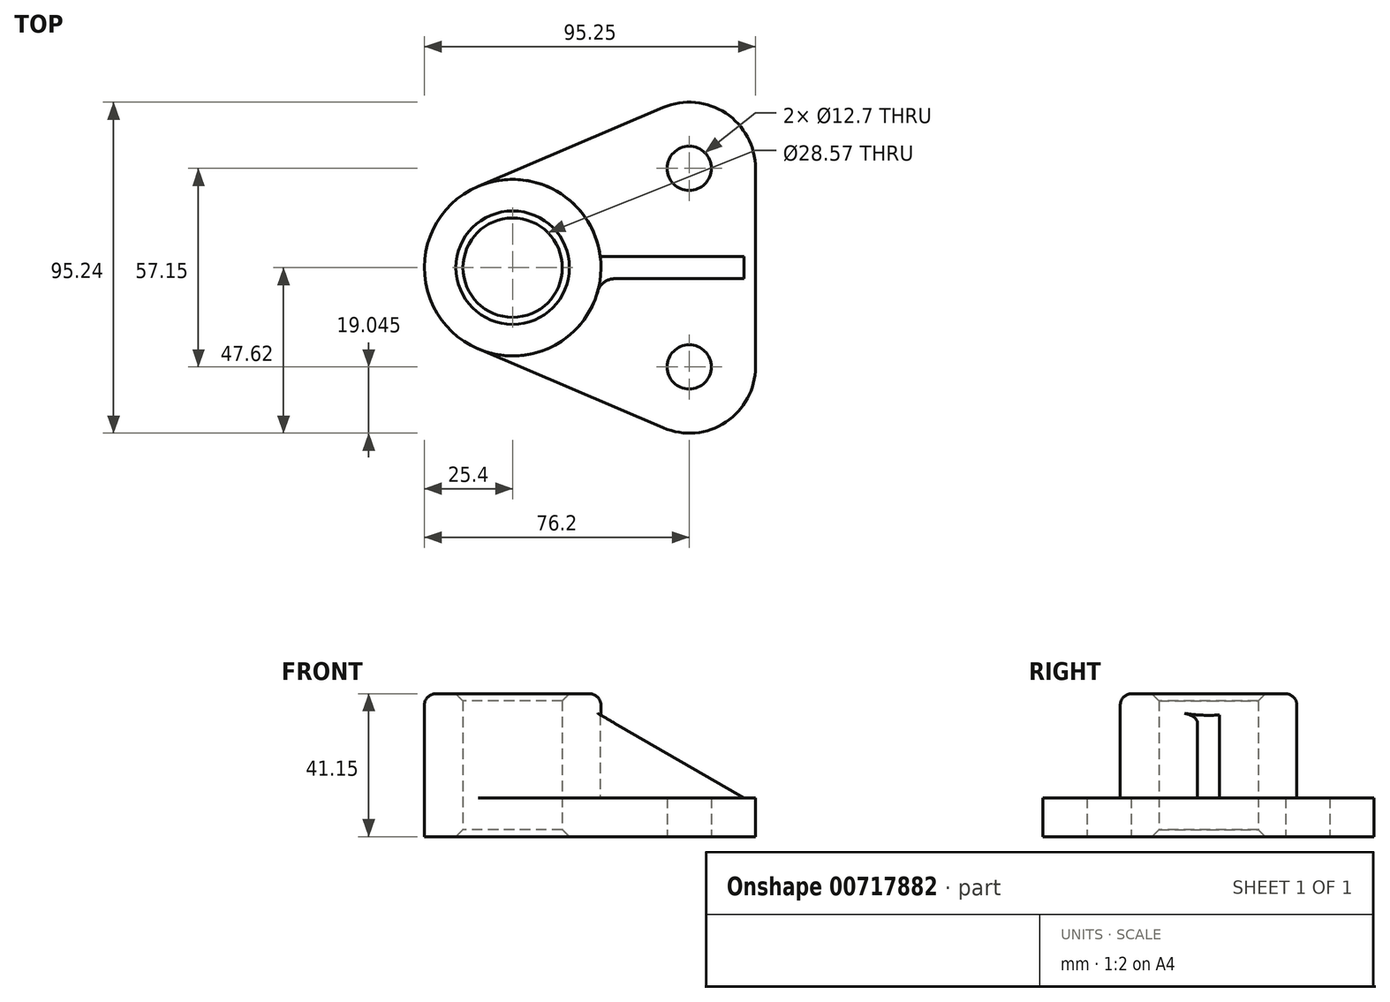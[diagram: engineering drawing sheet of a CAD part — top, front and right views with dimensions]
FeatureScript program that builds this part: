
annotation { "Feature Type Name" : "Feature", "Feature Type Description" : "" }
export const myFeature = defineFeature(function(context is Context, id is Id, definition is map)
    precondition{}
    {
        {
            var Q0;
            Q0=qCreatedBy(makeId("Top.planeOp"),FACE);
            var sketch = newSketch(context, id + "F0", { "sketchPlane" : qUnion([Q0])});
            skCircle(sketch, "E0", {"center": v(0, 0) * mm, "radius": 25.4 * mm});
            skCircle(sketch, "E1", {"center": v(0, 0) * mm, "radius": 14.29 * mm});
            skLineSegment(sketch, "E2", {"start": v(0, 0) * mm, "end": v(75.31, 0) * mm, "construction": true});
            skCircle(sketch, "E3", {"center": v(50.8, -28.58) * mm, "radius": 6.35 * mm});
            skArc(sketch, "E4", {"start": v(43.33, -46.1) * mm, "mid": v(61.3, -44.47) * mm, "end": v(69.85, -28.58) * mm});
            skArc(sketch, "E5.MirrorC", {"start": v(43.33, 46.1) * mm, "mid": v(61.3, 44.47) * mm, "end": v(69.85, 28.58) * mm});
            skCircle(sketch, "E6.MirrorC", {"center": v(50.8, 28.58) * mm, "radius": 6.35 * mm});
            skLineSegment(sketch, "E7", {"start": v(-9.97, 23.36) * mm, "end": v(43.33, 46.1) * mm});
            skLineSegment(sketch, "E8.MirrorCS", {"start": v(-9.97, -23.36) * mm, "end": v(43.33, -46.1) * mm});
            skLineSegment(sketch, "E9", {"start": v(69.85, 28.58) * mm, "end": v(69.85, -28.58) * mm});
            skSolve(sketch);
        }
        {
            var Q0;
            Q0=makeQuery(id+"F0.imprint","IMPRINT",FACE,{"disambiguationData":[TD([[makeQuery(id+"F0.imprint","IMPRINT",EDGE,{"derivedFrom":sQuery(id+"F0.wireOp",EDGE,"E1")}),-1.0]])]});
            extrude(context, id + "F1", {"entities" : qUnion([Q0]), "depth" : 41.15 * mm, "offsetDistance" : 25.4 * mm});
        }
        {
            var Q0;
            Q0=makeQuery(id+"F0.imprint","IMPRINT",FACE,{"disambiguationData":[TD([[makeQuery(id+"F0.imprint","IMPRINT",EDGE,{"derivedFrom":sQuery(id+"F0.wireOp",EDGE,"E3")}),-1.0]])]});
            extrude(context, id + "F2", {"entities" : qUnion([Q0]), "operationType" : NewBodyOperationType.ADD, "depth" : 11.18 * mm, "offsetDistance" : 25.4 * mm});
        }
        {
            var Q0;
            Q0=qCreatedBy(makeId("Front.planeOp"),FACE);
            var sketch = newSketch(context, id + "F3", { "sketchPlane" : qUnion([Q0])});
            skLineSegment(sketch, "E10", {"start": v(66.55, 11.18) * mm, "end": v(69.85, 11.18) * mm});
            skLineSegment(sketch, "E11", {"start": v(66.55, 11.18) * mm, "end": v(24.18, 11.18) * mm});
            skLineSegment(sketch, "E12", {"start": v(66.55, 11.18) * mm, "end": v(24.18, 35.64) * mm});
            skLineSegment(sketch, "E13", {"start": v(24.18, 35.64) * mm, "end": v(24.18, 11.18) * mm});
            skSolve(sketch);
        }
        {
            var Q0;
            Q0=makeQuery(id+"F3.imprint","IMPRINT",FACE,{"disambiguationData":[TD([[makeQuery(id+"F3.imprint","IMPRINT",EDGE,{"derivedFrom":sQuery(id+"F3.wireOp",EDGE,"E11")}),-1.0]])]});
            extrude(context, id + "F4", {"entities" : qUnion([Q0]), "operationType" : NewBodyOperationType.ADD, "depth" : 3.17 * mm, "offsetDistance" : 25.4 * mm});
        }
        {
            var Q0;
            Q0=makeQuery(id+"F1.opExtrude","SWEPT_BODY",BODY,{"disambiguationData":[OSD([sQuery(id+"F0.wireOp",EDGE,"E0"),sQuery(id+"F0.wireOp",EDGE,"E1")])]});
            var Q1;
            Q1=qCreatedBy(makeId("Front.planeOp"),FACE);
            mirror(context, id + "F5", {"operationType" : NewBodyOperationType.ADD, "entities" : qUnion([Q0]), "mirrorPlane" : qUnion([Q1])});
        }
        {
            var Q0;
            {var subQ0=sQuery(id+"F0.wireOp",EDGE,"E0");var subQ1=sQuery(id+"F0.wireOp",EDGE,"E8.MirrorCS");Q0=makeQuery(id+"F4.boolean.opBoolean","SPLIT",EDGE,{"disambiguationData":[TD([makeQuery(id+"F2.opExtrude","SWEPT_FACE",FACE,{"disambiguationData":[OSD([subQ1])]})])],"derivedFrom":makeQuery(id+"F2.opExtrude","CAP_EDGE",EDGE,{"disambiguationData":[OSD([subQ0])],"isStart":false})});}
            var Q1;
            {var subQ0=sQuery(id+"F0.wireOp",EDGE,"E0");var subQ1=sQuery(id+"F0.wireOp",EDGE,"E7");Q1=makeQuery(id+"F4.boolean.opBoolean","SPLIT",EDGE,{"disambiguationData":[TD([makeQuery(id+"F2.opExtrude","SWEPT_FACE",FACE,{"disambiguationData":[OSD([subQ1])]})])],"derivedFrom":makeQuery(id+"F2.opExtrude","CAP_EDGE",EDGE,{"disambiguationData":[OSD([subQ0])],"isStart":false})});}
            var Q2;
            Q2=makeQuery(id+"F4.boolean.opBoolean","INTERSECT",EDGE,{"derivedFrom":[makeQuery(id+"F1.opExtrude","SWEPT_FACE",FACE,{"disambiguationData":[OSD([sQuery(id+"F0.wireOp",EDGE,"E0")])]}),makeQuery(id+"F4.opExtrude","CAP_FACE",FACE,{"disambiguationData":[OSD([sQuery(id+"F3.wireOp",EDGE,"E11"),sQuery(id+"F3.wireOp",EDGE,"E12"),sQuery(id+"F3.wireOp",EDGE,"E13")])],"isStart":false})]});
            var Q3;
            Q3=makeQuery(id+"F4.opExtrude","CAP_EDGE",EDGE,{"disambiguationData":[OSD([sQuery(id+"F3.wireOp",EDGE,"E11")])],"isStart":false});
            var Q4;
            Q4=makeQuery(id+"F5.opPattern","COPY",EDGE,{"derivedFrom":makeQuery(id+"F4.boolean.opBoolean","INTERSECT",EDGE,{"derivedFrom":[makeQuery(id+"F1.opExtrude","SWEPT_FACE",FACE,{"disambiguationData":[OSD([sQuery(id+"F0.wireOp",EDGE,"E0")])]}),makeQuery(id+"F4.opExtrude","CAP_FACE",FACE,{"disambiguationData":[OSD([sQuery(id+"F3.wireOp",EDGE,"E11"),sQuery(id+"F3.wireOp",EDGE,"E12"),sQuery(id+"F3.wireOp",EDGE,"E13")])],"isStart":false})]}),"instanceName":"1"});
            var Q5;
            Q5=makeQuery(id+"F5.opPattern","COPY",EDGE,{"derivedFrom":makeQuery(id+"F4.opExtrude","CAP_EDGE",EDGE,{"disambiguationData":[OSD([sQuery(id+"F3.wireOp",EDGE,"E11")])],"isStart":false}),"instanceName":"1"});
            fillet(context, id + "F6", {"entities" : qUnion([Q0, Q1, Q2, Q3, Q4, Q5]), "radius" : 5.08 * mm, "tangentPropagation" : true, "allowEdgeOverflow" : false});
        }
        {
            var Q0;
            Q0=makeQuery(id+"F1.opExtrude","CAP_EDGE",EDGE,{"disambiguationData":[OSD([sQuery(id+"F0.wireOp",EDGE,"E0")])],"isStart":false});
            fillet(context, id + "F7", {"entities" : qUnion([Q0]), "radius" : 3.3 * mm, "tangentPropagation" : true, "allowEdgeOverflow" : false});
        }
        {
            var Q0;
            Q0=makeQuery(id+"F1.opExtrude","CAP_EDGE",EDGE,{"disambiguationData":[OSD([sQuery(id+"F0.wireOp",EDGE,"E1")])],"isStart":false});
            var Q1;
            Q1=makeQuery(id+"F1.opExtrude","CAP_EDGE",EDGE,{"disambiguationData":[OSD([sQuery(id+"F0.wireOp",EDGE,"E1")])],"isStart":true});
            chamfer(context, id + "F8", {"entities" : qUnion([Q0, Q1]), "chamferType" : ChamferType.OFFSET_ANGLE, "width" : 2.03 * mm, "oppositeDirection" : false, "angle" : 45 * degree, "tangentPropagation" : true});
        }
    });
